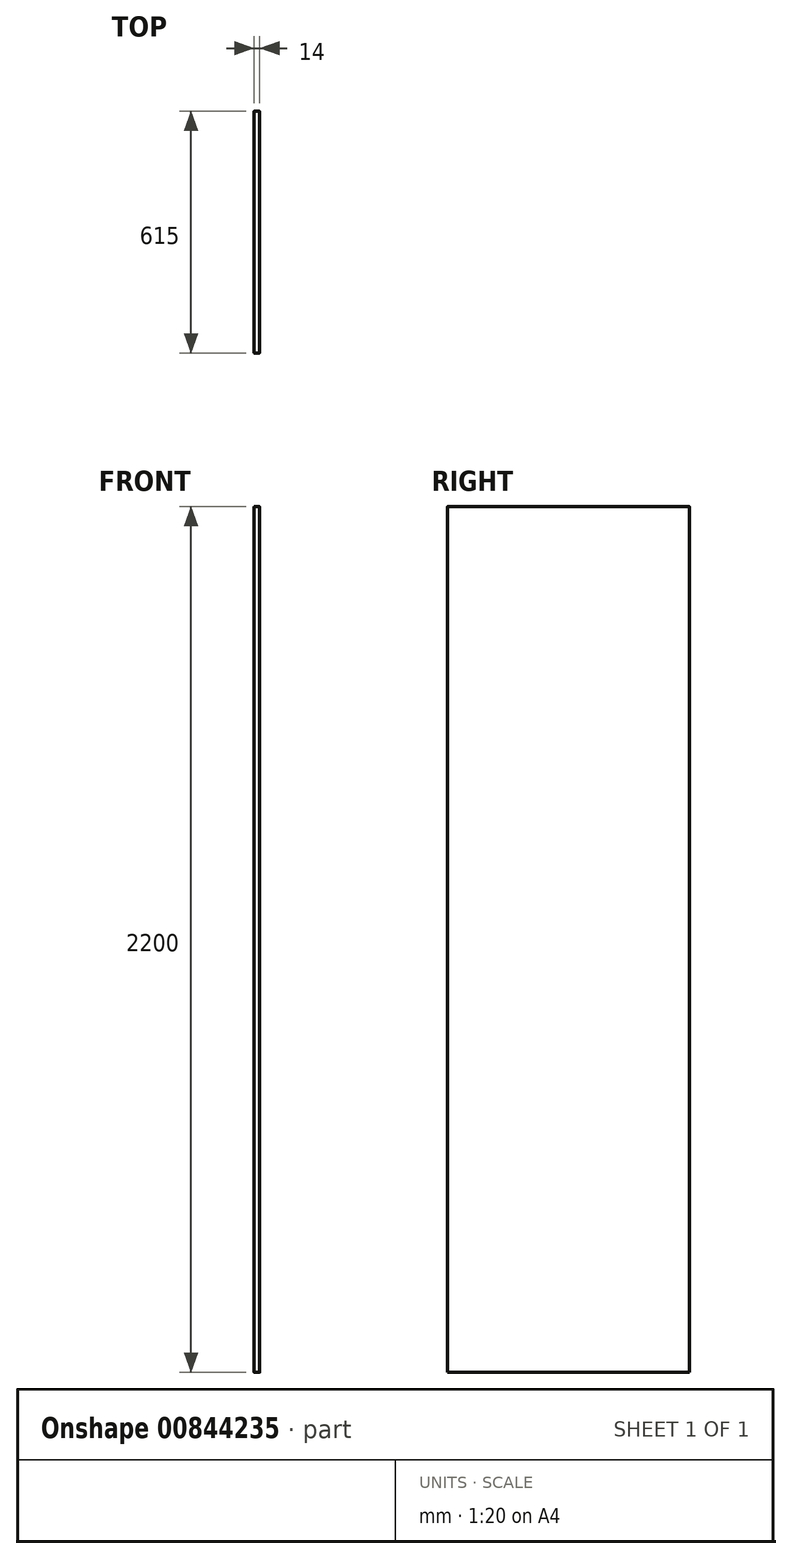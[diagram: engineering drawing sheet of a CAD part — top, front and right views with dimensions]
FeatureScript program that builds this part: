
annotation { "Feature Type Name" : "Feature", "Feature Type Description" : "" }
export const myFeature = defineFeature(function(context is Context, id is Id, definition is map)
    precondition{}
    {
        {
            var Q0;
            Q0=qCreatedBy(makeId("Right.planeOp"),FACE);
            var sketch = newSketch(context, id + "F0", { "sketchPlane" : qUnion([Q0])});
            skLineSegment(sketch, "E0.bottom", {"start": v(0, 0) * mm, "end": v(-45.38, 0) * mm});
            skLineSegment(sketch, "E0.top", {"start": v(0, 30.28) * mm, "end": v(-45.38, 30.28) * mm});
            skLineSegment(sketch, "E0.left", {"start": v(0, 0) * mm, "end": v(0, 30.28) * mm});
            skLineSegment(sketch, "E0.right", {"start": v(-45.38, 0) * mm, "end": v(-45.38, 30.28) * mm});
            skSolve(sketch);
        }
        {
            var Q0;
            Q0=makeQuery(id+"F0.imprint","IMPRINT",FACE,{"disambiguationData":[TD([[makeQuery(id+"F0.imprint","IMPRINT",EDGE,{"derivedFrom":sQuery(id+"F0.wireOp",EDGE,"E0.bottom")}),-1.0]])]});
            extrude(context, id + "F1", {"entities" : qUnion([Q0]), "depth" : 14 * mm, "offsetDistance" : 25 * mm});
        }
        {
            var Q0;
            Q0=makeQuery(id+"F1.opExtrude","SWEPT_FACE",FACE,{"disambiguationData":[OSD([sQuery(id+"F0.wireOp",EDGE,"E0.left")])]});
            extrude(context, id + "F2", {"entities" : qUnion([Q0]), "operationType" : NewBodyOperationType.ADD, "oppositeDirection" : true, "depth" : 615 * mm, "offsetDistance" : 25 * mm});
        }
        {
            var Q0;
            {var subQ0=sQuery(id+"F0.wireOp",EDGE,"E0.bottom");Q0=makeQuery(id+"F2.boolean.opBoolean","MERGE",FACE,{"derivedFrom":[makeQuery(id+"F1.opExtrude","SWEPT_FACE",FACE,{"disambiguationData":[OSD([subQ0])]}),makeQuery(id+"F2.opExtrude","SWEPT_FACE",FACE,{"disambiguationData":[OSD([subQ0,sQuery(id+"F0.wireOp",EDGE,"E0.left")])]})]});}
            extrude(context, id + "F3", {"entities" : qUnion([Q0]), "operationType" : NewBodyOperationType.ADD, "oppositeDirection" : true, "depth" : 2200 * mm, "offsetDistance" : 25 * mm});
        }
        {
            var Q0;
            {var subQ0=sQuery(id+"F0.wireOp",EDGE,"E0.left");var subQ1=sQuery(id+"F0.wireOp",EDGE,"E0.bottom");Q0=makeQuery(id+"F3.boolean.opBoolean","MERGE",FACE,{"derivedFrom":[makeQuery(id+"F2.boolean.opBoolean","MERGE",FACE,{"derivedFrom":[makeQuery(id+"F1.opExtrude","CAP_FACE",FACE,{"disambiguationData":[OSD([subQ1,sQuery(id+"F0.wireOp",EDGE,"E0.top"),subQ0,sQuery(id+"F0.wireOp",EDGE,"E0.right")])],"isStart":true}),makeQuery(id+"F2.opExtrude","SWEPT_FACE",FACE,{"disambiguationData":[OSD([subQ0]),TDD([makeQuery(id+"F1.opExtrude","CAP_EDGE",EDGE,{"disambiguationData":[OSD([subQ0])],"isStart":true})])]})]}),makeQuery(id+"F3.opExtrude","SWEPT_FACE",FACE,{"disambiguationData":[OSD([subQ1,subQ0]),TDD([makeQuery(id+"F2.boolean.opBoolean","MERGE",EDGE,{"derivedFrom":[makeQuery(id+"F1.opExtrude","CAP_EDGE",EDGE,{"disambiguationData":[OSD([subQ1])],"isStart":true}),makeQuery(id+"F2.opExtrude","SWEPT_EDGE",EDGE,{"disambiguationData":[OSD([subQ1,subQ0]),TDD([makeQuery(id+"F1.opExtrude","CAP_VERTEX",VERTEX,{"disambiguationData":[OSD([subQ1,subQ0])],"isStart":true})])]})]})])]})]});}
            var Q1;
            {var subQ0=sQuery(id+"F0.wireOp",EDGE,"E0.left");var subQ1=sQuery(id+"F0.wireOp",EDGE,"E0.bottom");Q1=makeQuery(id+"F3.boolean.opBoolean","MERGE",FACE,{"derivedFrom":[makeQuery(id+"F2.boolean.opBoolean","MERGE",FACE,{"derivedFrom":[makeQuery(id+"F1.opExtrude","CAP_FACE",FACE,{"disambiguationData":[OSD([subQ1,sQuery(id+"F0.wireOp",EDGE,"E0.top"),subQ0,sQuery(id+"F0.wireOp",EDGE,"E0.right")])],"isStart":false}),makeQuery(id+"F2.opExtrude","SWEPT_FACE",FACE,{"disambiguationData":[OSD([subQ0]),TDD([makeQuery(id+"F1.opExtrude","CAP_EDGE",EDGE,{"disambiguationData":[OSD([subQ0])],"isStart":false})])]})]}),makeQuery(id+"F3.opExtrude","SWEPT_FACE",FACE,{"disambiguationData":[OSD([subQ1,subQ0]),TDD([makeQuery(id+"F2.boolean.opBoolean","MERGE",EDGE,{"derivedFrom":[makeQuery(id+"F1.opExtrude","CAP_EDGE",EDGE,{"disambiguationData":[OSD([subQ1])],"isStart":false}),makeQuery(id+"F2.opExtrude","SWEPT_EDGE",EDGE,{"disambiguationData":[OSD([subQ1,subQ0]),TDD([makeQuery(id+"F1.opExtrude","CAP_VERTEX",VERTEX,{"disambiguationData":[OSD([subQ1,subQ0])],"isStart":false})])]})]})])]})]});}
            fillet(context, id + "F4", {"entities" : qUnion([Q0, Q1]), "radius" : 1 * mm, "tangentPropagation" : true, "allowEdgeOverflow" : false});
        }
    });
